# Revit family: Nonstop
name_source: partatom
category: Мебель
revit_build: Autodesk Revit 2017 (Build: 20160225_1515(x64)
units: mm (PartAtom-declared; Revit-internal decimal feet)

## family parameters
Всегда вертикально = Да
Заголовок OmniClass = General Furniture and Specialties
На основе рабочей плоскости = Нет
Номер OmniClass = 23.40.20.00
Общий = Нет
При загрузке вырезать с полостями = Нет
Точка расчета площади = Нет

## types (7) — shared parameters
Fabric = Skandiform Fabric
Leg = Skandiform Chrome
Изготовитель = Skandiform AB
Ключевая пометка = XBF.4
Комментарии к типоразмеру = Created by Astacus AB
Описание = Division Bench. Four different section parts (straight, curved with wide back, curved with narrow back and corner unit) are put together according to your preference. Complete with arm and leg.

## per-type parameters (varying)
| type | URL |
| SA-380 | http://www.biminfo.se |
| SA-381 | http://www.biminfo.se |
| SA-382 | http://www.biminfo.se |
| SA-383 | http://www.biminfo.se |
| SA-384 | http://www.biminfo.se |
| SA-386 | http://www.biminfo.se |
| SA-385 | http://file-system.ru |

note: column(s) folded — value = type name in every type: Type, Группа модели

## geometry (parser evidence)
native form markers: Blend x18, Sweep x16
no freeform markers — native parametric forms only
